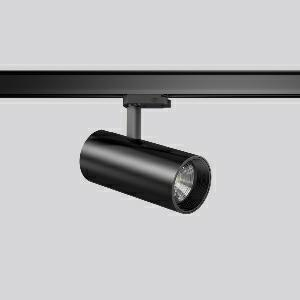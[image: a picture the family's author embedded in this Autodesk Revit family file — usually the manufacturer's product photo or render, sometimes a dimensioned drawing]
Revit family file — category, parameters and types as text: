
# Revit family: deecos_s_mini_742209_003_3_a809
name_source: partatom
category: Lighting Fixtures
units: mm (PartAtom-declared; Revit-internal decimal feet)

## family parameters
Cut with Voids When Loaded = No
Host = Face
Light Source = No
Part Type = Normal
Room Calculation Point = No
Round Connector Dimension = Use Diameter
Shared = No

## types (1)
- DEECOS S mini (1 x LED Modul 935, 3300 lm, 3500)
    Apparent Load = 29 VA
    Approval mark = CE
    CIE Flux Codes = 80 99 100 100 100
    Color Rendering = 92
    Color Temperature = 3500
    Default Elevation = 1800 mm
    Description = Series: DEECOS S mini
LED surface-mounted projector in modern design with no visible cooling ribs. Housing: die-cast aluminium, powder-coated. Rotation range: 356°. Swivel range: 90°. Black plastic ring and recessed LED to prevent glare from the side. Optical assembly with lens made of plastic (polycarbonate) for the best homogeneous light distribution - can be changed without tools. Best colour rendering index Ra>90. With multi adaptor for 3-circuit tracks 230 V. Suitable for Track on ceiling, Wall track. High quality converter without flickering and stroboscopic effect. The following accessories can be mounted without use of tools: interchangeable lenses, decorative glasses, honeycomb louvre, clear and frosted diffusers, white interchangeable plastic ring. 
Colour: deep black, matt (RAL 9005)
Diameter: 87 mm
Height: 214 mm
Lamp: LED
Socket: without socket
Colour temperature: 3500K
Colour rendering index (CRI): 92
System power: 29 W
Rated luminous flux: 3300 lm
Luminous efficiency: 114 lm/W
Control gear: Regulated power supply
Protection class: I
Type of protection: IP 20
    Height = 214 mm
    Lamp = 1 x LED Modul 935
    Lamp Light Flux = 3300 lm
    Lamp count = 1
    Length = 87 mm
    Lifetime = 50000 h
    Luminous efficacy = 114 lm/W
    Manufacturer = RZB
    ModVariant = No
    Model = 742209.003.3
    Mounting Place = Ceiling
    Mounting Type = Rail mounted
    Number of Poles = 1
    OnlyDefault = Yes
    Power Factor = 1
    Product Name = DEECOS S mini
    Product group = Track mounted projectors
    ProductGroupID = 301
    Protection Class = Protection class I
    Protection Degree = IP 20
    RLX_Detail_Level = 1
    RLX_Emergency_Light_Flux = 0 lm
    RLX_Emergency_Type = 0
    RLX_Emergency_Type_DB = No
    RlxData = <blob elided: 38773 chars, md5=5d56243f>
    Socket = socket
    Standby Power = 0 W
    System Light Flux = 3300 lm
    System Power = 29 W
    Type Comments = Product without accessories
    Type Image = 741930.003.jpg
    URL = http://relux.com
    VarID = ---
    Voltage = 230 V
    Voltage Range = 220-240 V
    Weight = 0.00 kg
    Width = 0 mm  [stored 0 ft]

note: [stored X ft] marks values corroborated as IEEE doubles in the binary element streams (Revit-internal decimal feet)

## geometry (parser evidence)
native form markers: Blend x4, Sweep x12
no freeform markers — native parametric forms only
